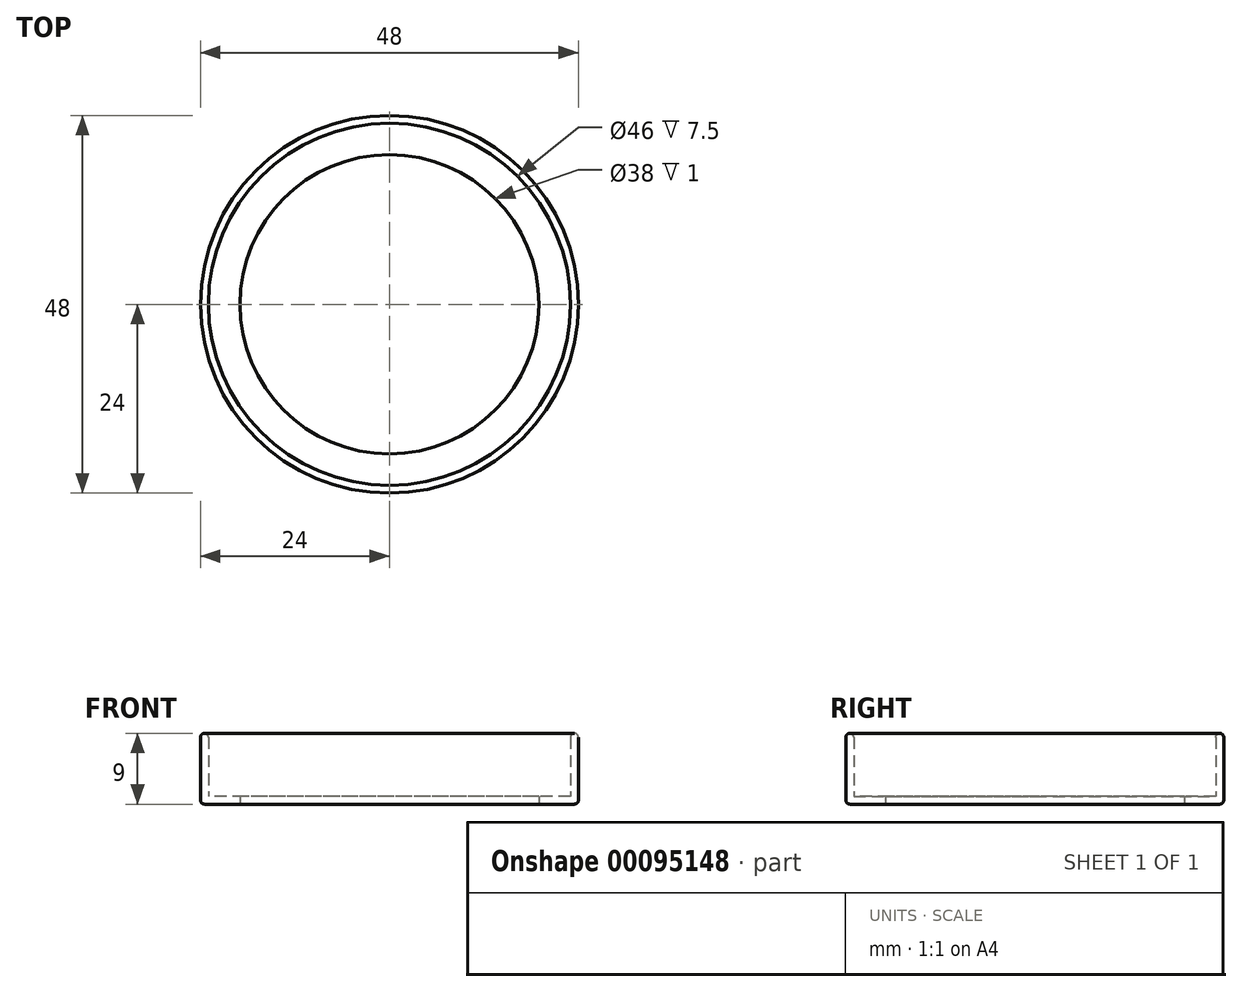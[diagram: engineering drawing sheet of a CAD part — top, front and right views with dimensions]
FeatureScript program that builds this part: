
annotation { "Feature Type Name" : "Feature", "Feature Type Description" : "" }
export const myFeature = defineFeature(function(context is Context, id is Id, definition is map)
    precondition{}
    {
        {
            var Q0;
            Q0=qCreatedBy(makeId("Top.planeOp"),FACE);
            var sketch = newSketch(context, id + "F0", { "sketchPlane" : qUnion([Q0])});
            skCircle(sketch, "E0", {"center": v(0, 0) * mm, "radius": 24 * mm});
            skCircle(sketch, "E1", {"center": v(0, 0) * mm, "radius": 23 * mm});
            skCircle(sketch, "E2", {"center": v(0, 0) * mm, "radius": 19 * mm});
            skSolve(sketch);
        }
        {
            var Q0;
            Q0=makeQuery(id+"F0.imprint","IMPRINT",FACE,{"disambiguationData":[TD([[makeQuery(id+"F0.imprint","IMPRINT",EDGE,{"derivedFrom":sQuery(id+"F0.wireOp",EDGE,"E0")}),1.0]])]});
            extrude(context, id + "F1", {"entities" : qUnion([Q0]), "depth" : 9 * mm});
        }
        {
            var Q0;
            Q0=makeQuery(id+"F0.imprint","IMPRINT",FACE,{"disambiguationData":[TD([[makeQuery(id+"F0.imprint","IMPRINT",EDGE,{"derivedFrom":sQuery(id+"F0.wireOp",EDGE,"E1")}),1.0]])]});
            extrude(context, id + "F2", {"entities" : qUnion([Q0]), "operationType" : NewBodyOperationType.ADD, "depth" : 1 * mm});
        }
        {
            var Q0;
            Q0=makeQuery(id+"F1.opExtrude","CAP_EDGE",EDGE,{"disambiguationData":[OSD([sQuery(id+"F0.wireOp",EDGE,"E0")])],"isStart":true});
            var Q1;
            Q1=makeQuery(id+"F1.opExtrude","CAP_EDGE",EDGE,{"disambiguationData":[OSD([sQuery(id+"F0.wireOp",EDGE,"E0")])],"isStart":false});
            var Q2;
            Q2=makeQuery(id+"F1.opExtrude","CAP_EDGE",EDGE,{"disambiguationData":[OSD([sQuery(id+"F0.wireOp",EDGE,"E1")])],"isStart":false});
            fillet(context, id + "F3", {"entities" : qUnion([Q0, Q1, Q2]), "radius" : .5 * mm, "tangentPropagation" : true, "allowEdgeOverflow" : false});
        }
    });
